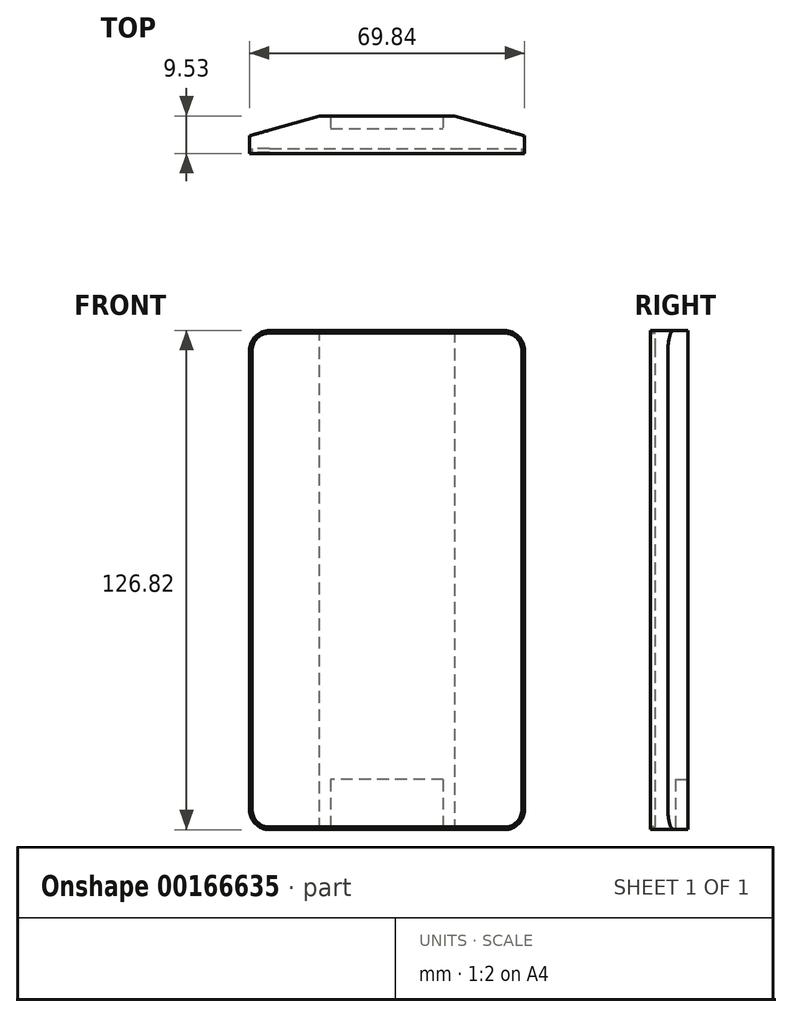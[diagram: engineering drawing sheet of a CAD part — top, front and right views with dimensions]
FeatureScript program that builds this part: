
annotation { "Feature Type Name" : "Feature", "Feature Type Description" : "" }
export const myFeature = defineFeature(function(context is Context, id is Id, definition is map)
    precondition{}
    {
        {
            var Q0;
            Q0=qCreatedBy(makeId("Front.planeOp"),FACE);
            var sketch = newSketch(context, id + "F0", { "sketchPlane" : qUnion([Q0])});
            skLineSegment(sketch, "E0.bottom", {"start": v(34.93, 63.4) * mm, "end": v(-34.93, 63.4) * mm});
            skLineSegment(sketch, "E0.top", {"start": v(34.93, -63.4) * mm, "end": v(-34.93, -63.4) * mm});
            skLineSegment(sketch, "E0.left", {"start": v(34.93, 63.4) * mm, "end": v(34.93, -63.4) * mm});
            skLineSegment(sketch, "E0.right", {"start": v(-34.93, 63.4) * mm, "end": v(-34.93, -63.4) * mm});
            skPoint(sketch, "E0.middle", {"position": v(0, 0) * mm});
            skSolve(sketch);
        }
        {
            var Q0;
            Q0 = qSketchRegion(id + "F0", true);
            extrude(context, id + "F1", {"entities" : qUnion([Q0]), "depth" : 9.52 * mm});
        }
        {
            var Q0;
            Q0=makeQuery(id+"F1.opExtrude","CAP_EDGE",EDGE,{"disambiguationData":[OSD([sQuery(id+"F0.wireOp",EDGE,"E0.left")])],"isStart":true});
            var Q1;
            Q1=makeQuery(id+"F1.opExtrude","CAP_EDGE",EDGE,{"disambiguationData":[OSD([sQuery(id+"F0.wireOp",EDGE,"E0.right")])],"isStart":true});
            chamfer(context, id + "F2", {"entities" : qUnion([Q0, Q1]), "chamferType" : ChamferType.TWO_OFFSETS, "width1" : 17.78 * mm, "oppositeDirection" : false, "width2" : 5.08 * mm, "tangentPropagation" : true});
        }
        {
            var Q0;
            Q0=makeQuery(id+"F1.opExtrude","SWEPT_EDGE",EDGE,{"disambiguationData":[OSD([sQuery(id+"F0.wireOp",EDGE,"E0.bottom"),sQuery(id+"F0.wireOp",EDGE,"E0.left")])]});
            var Q1;
            Q1=makeQuery(id+"F1.opExtrude","SWEPT_EDGE",EDGE,{"disambiguationData":[OSD([sQuery(id+"F0.wireOp",EDGE,"E0.bottom"),sQuery(id+"F0.wireOp",EDGE,"E0.right")])]});
            var Q2;
            Q2=makeQuery(id+"F1.opExtrude","SWEPT_EDGE",EDGE,{"disambiguationData":[OSD([sQuery(id+"F0.wireOp",EDGE,"E0.top"),sQuery(id+"F0.wireOp",EDGE,"E0.right")])]});
            var Q3;
            Q3=makeQuery(id+"F1.opExtrude","SWEPT_EDGE",EDGE,{"disambiguationData":[OSD([sQuery(id+"F0.wireOp",EDGE,"E0.top"),sQuery(id+"F0.wireOp",EDGE,"E0.left")])]});
            fillet(context, id + "F3", {"entities" : qUnion([Q0, Q1, Q2, Q3]), "radius" : 5.08 * mm, "tangentPropagation" : true, "allowEdgeOverflow" : false});
        }
        {
            var Q0;
            Q0=makeQuery(id+"F1.opExtrude","CAP_FACE",FACE,{"disambiguationData":[OSD([sQuery(id+"F0.wireOp",EDGE,"E0.bottom"),sQuery(id+"F0.wireOp",EDGE,"E0.top"),sQuery(id+"F0.wireOp",EDGE,"E0.left"),sQuery(id+"F0.wireOp",EDGE,"E0.right")])],"isStart":false});
            var sketch = newSketch(context, id + "F4", { "sketchPlane" : qUnion([Q0])});
            skArc(sketch, "E1.0", {"start": v(29.85, -62.77) * mm, "mid": v(32.99, -61.47) * mm, "end": v(34.3, -58.33) * mm});
            skLineSegment(sketch, "E1.1", {"start": v(-29.85, -62.77) * mm, "end": v(29.85, -62.77) * mm});
            skLineSegment(sketch, "E1.2", {"start": v(34.3, -58.33) * mm, "end": v(34.3, 58.33) * mm});
            skArc(sketch, "E1.3", {"start": v(-34.3, -58.33) * mm, "mid": v(-32.99, -61.47) * mm, "end": v(-29.85, -62.77) * mm});
            skArc(sketch, "E1.4", {"start": v(34.3, 58.33) * mm, "mid": v(32.99, 61.47) * mm, "end": v(29.85, 62.77) * mm});
            skLineSegment(sketch, "E1.5", {"start": v(29.85, 62.77) * mm, "end": v(-29.84, 62.77) * mm});
            skArc(sketch, "E1.6", {"start": v(-29.84, 62.77) * mm, "mid": v(-32.99, 61.47) * mm, "end": v(-34.3, 58.33) * mm});
            skLineSegment(sketch, "E1.7", {"start": v(-34.3, 58.33) * mm, "end": v(-34.3, -58.33) * mm});
            skSolve(sketch);
        }
        {
            var Q0;
            Q0=makeQuery(id+"F4.imprint","IMPRINT",FACE,{"disambiguationData":[TD([[makeQuery(id+"F4.imprint","IMPRINT",EDGE,{"derivedFrom":sQuery(id+"F4.wireOp",EDGE,"E1.0")}),1.0]])]});
            extrude(context, id + "F5", {"entities" : qUnion([Q0]), "operationType" : NewBodyOperationType.REMOVE, "oppositeDirection" : true, "depth" : 1.27 * mm});
        }
        {
            var Q0;
            Q0=makeQuery(id+"F5.boolean.opBoolean","COPY",FACE,{"derivedFrom":makeQuery(id+"F5.opExtrude","CAP_FACE",FACE,{"disambiguationData":[OSD([sQuery(id+"F4.wireOp",EDGE,"E1.0"),sQuery(id+"F4.wireOp",EDGE,"E1.1"),sQuery(id+"F4.wireOp",EDGE,"E1.2"),sQuery(id+"F4.wireOp",EDGE,"E1.3"),sQuery(id+"F4.wireOp",EDGE,"E1.4"),sQuery(id+"F4.wireOp",EDGE,"E1.5"),sQuery(id+"F4.wireOp",EDGE,"E1.6"),sQuery(id+"F4.wireOp",EDGE,"E1.7")])],"isStart":false})});
            var Q1;
            Q1=makeQuery(id+"F1.opExtrude","CAP_FACE",FACE,{"disambiguationData":[OSD([sQuery(id+"F0.wireOp",EDGE,"E0.bottom"),sQuery(id+"F0.wireOp",EDGE,"E0.top"),sQuery(id+"F0.wireOp",EDGE,"E0.left"),sQuery(id+"F0.wireOp",EDGE,"E0.right")])],"isStart":false});
            extrude(context, id + "F6", {"entities" : qUnion([Q0]), "endBoundEntityFace" : qUnion([Q1]), "depth" : 1.02 * mm});
        }
        {
            var Q0;
            Q0=makeQuery(id+"F1.opExtrude","CAP_FACE",FACE,{"disambiguationData":[OSD([sQuery(id+"F0.wireOp",EDGE,"E0.bottom"),sQuery(id+"F0.wireOp",EDGE,"E0.top"),sQuery(id+"F0.wireOp",EDGE,"E0.left"),sQuery(id+"F0.wireOp",EDGE,"E0.right")])],"isStart":true});
            var sketch = newSketch(context, id + "F7", { "sketchPlane" : qUnion([Q0])});
            skLineSegment(sketch, "E2.bottom", {"start": v(-14.29, -50.7) * mm, "end": v(14.29, -50.7) * mm});
            skLineSegment(sketch, "E2.top", {"start": v(-14.29, -76.1) * mm, "end": v(14.29, -76.1) * mm});
            skLineSegment(sketch, "E2.left", {"start": v(-14.29, -50.7) * mm, "end": v(-14.29, -76.1) * mm});
            skLineSegment(sketch, "E2.right", {"start": v(14.29, -50.7) * mm, "end": v(14.29, -76.1) * mm});
            skPoint(sketch, "E2.middle", {"position": v(0, -63.4) * mm});
            skSolve(sketch);
        }
        {
            var Q0;
            {var subQ0=sQuery(id+"F7.wireOp",EDGE,"E2.top");Q0=makeQuery(id+"F7.imprint","IMPRINT",FACE,{"disambiguationData":[TD([[makeQuery(id+"F7.imprint","IMPRINT",EDGE,{"derivedFrom":subQ0}),1.0]])]});}
            var Q1;
            {var subQ0=sQuery(id+"F7.wireOp",EDGE,"E2.bottom");Q1=makeQuery(id+"F7.imprint","IMPRINT",FACE,{"disambiguationData":[TD([[makeQuery(id+"F7.imprint","IMPRINT",EDGE,{"derivedFrom":subQ0}),-1.0]])]});}
            extrude(context, id + "F8", {"entities" : qUnion([Q0, Q1]), "operationType" : NewBodyOperationType.REMOVE, "oppositeDirection" : true, "depth" : 3.17 * mm});
        }
    });
